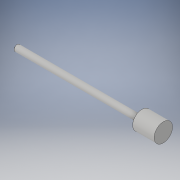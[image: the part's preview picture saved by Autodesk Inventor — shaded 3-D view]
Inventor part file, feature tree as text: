
AUTODESK INVENTOR PART (.ipt)
format: ipt  version: 2019 (Build 230136000, 136)  size: 145,920 bytes
history: native  units: mm
features: other x42, revolve x3, sketch x3
ambient origin geometry x8: Origin, YZ Plane, XZ Plane, XY Plane, X Axis, Y Axis, Z Axis, Center Point
bodies: Solid1 (feature_tree)
feature tree (48):
  revolve  "Revolution1"  Angle=360.0deg
  revolve  "Revolution2"  [1 undecoded]
  revolve  "Revolution3"  [1 undecoded]
  other  "a_XY"
  other  "a_YZ"
  other  "a_ZX"
  other  "a_X"
  other  "a_Y"
  other  "a_Z"
  other  "a_Center"
  other  "c1_XY"
  other  "c1_YZ"
  other  "c1_ZX"
  other  "c1_X"
  other  "c1_Y"
  other  "c1_Z"
  other  "c1_Center"
  other  "cc1_XY"
  other  "cc1_YZ"
  other  "cc1_ZX"
  other  "cc1_X"
  other  "cc1_Y"
  other  "cc1_Z"
  other  "cc1_Center"
  other  "cc2_XY"
  other  "cc2_YZ"
  other  "cc2_ZX"
  other  "cc2_X"
  other  "cc2_Y"
  other  "cc2_Z"
  other  "cc2_Center"
  other  "kk_XY"
  other  "kk_YZ"
  other  "kk_ZX"
  other  "kk_X"
  other  "kk_Y"
  other  "kk_Z"
  other  "kk_Center"
  other  "rod_XY"
  other  "rod_YZ"
  other  "rod_ZX"
  other  "rod_X"
  other  "rod_Y"
  other  "rod_Z"
  other  "rod_Center"
  sketch  "Sketch_1"  dims[d0=360.0deg d1=360.0deg]
  sketch  "Sketch_3"  dims[d2=360.0deg d3=0.0mm d4=0.0mm]
  sketch  "Sketch_4"
note: 2 required parameter values undecoded (feature->parameter linkage not recoverable at this tier; creation-order binding heuristic only, values carry confidence <= 0.55)